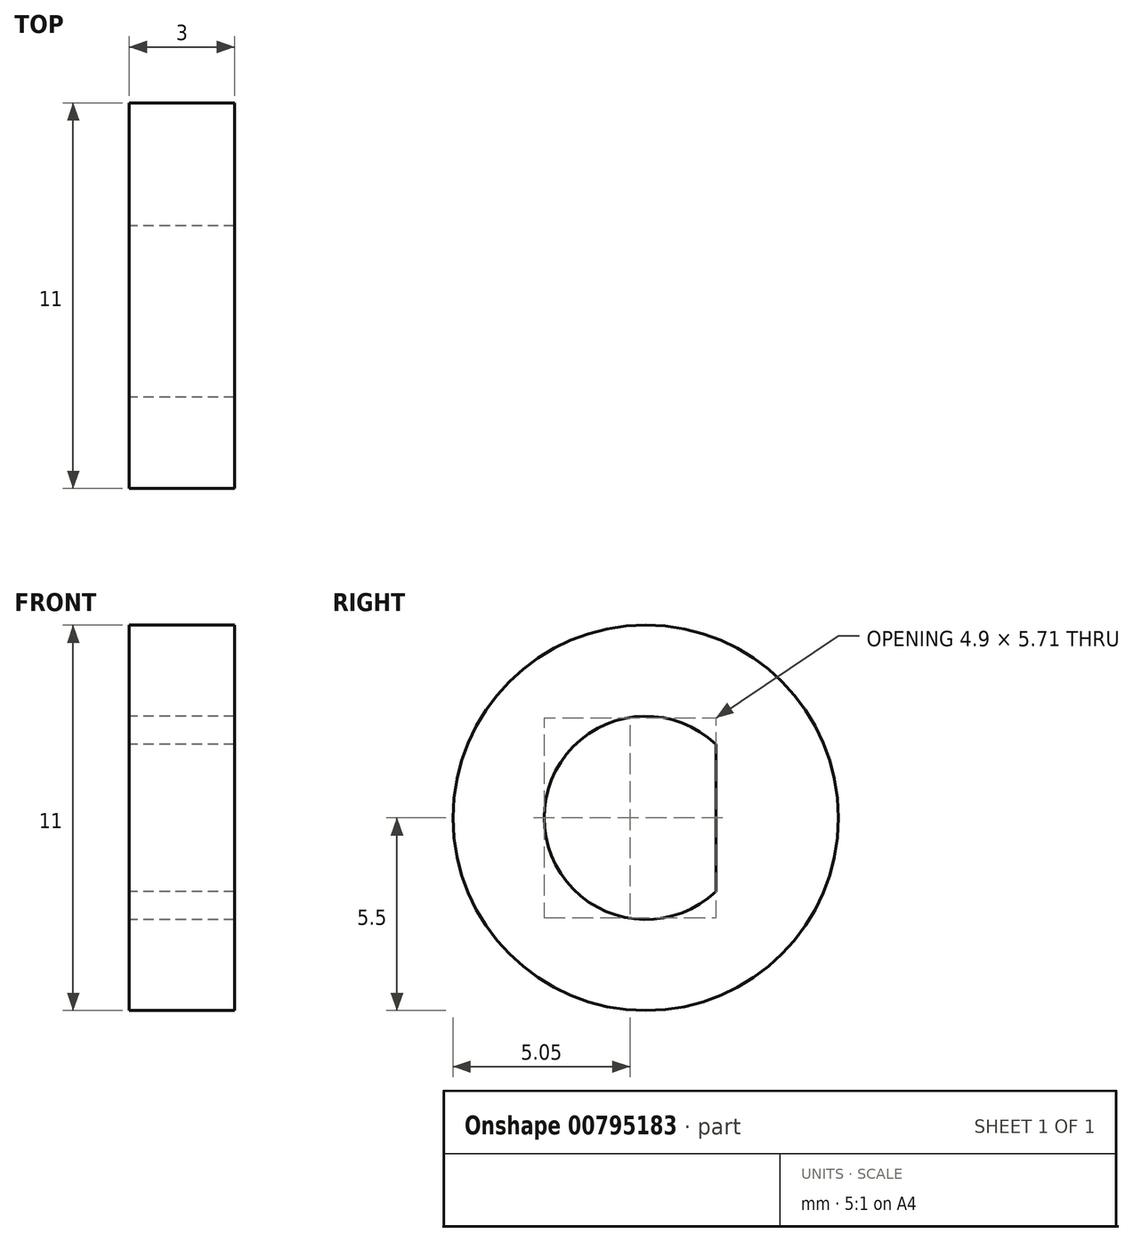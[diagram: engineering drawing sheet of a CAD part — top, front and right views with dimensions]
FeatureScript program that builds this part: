
annotation { "Feature Type Name" : "Feature", "Feature Type Description" : "" }
export const myFeature = defineFeature(function(context is Context, id is Id, definition is map)
    precondition{}
    {
        {
            var Q0;
            Q0=qCreatedBy(makeId("Right.planeOp"),FACE);
            var sketch = newSketch(context, id + "F0", { "sketchPlane" : qUnion([Q0])});
            skCircle(sketch, "E0", {"center": v(0, 0) * mm, "radius": 10.5 * mm, "construction": true});
            skCircle(sketch, "E1", {"center": v(0, 0) * mm, "radius": 2.9 * mm});
            skLineSegment(sketch, "E2", {"start": v(0, 0) * mm, "end": v(0, 12.5) * mm, "construction": true});
            skLineSegment(sketch, "E3", {"start": v(0, 12.5) * mm, "end": v(0.84, 10.47) * mm});
            skCircle(sketch, "E4", {"center": v(0, 0) * mm, "radius": 12.5 * mm, "construction": true});
            skLineSegment(sketch, "E5", {"start": v(0.84, 10.47) * mm, "end": v(2, 12.34) * mm});
            skLineSegment(sketch, "E6", {"start": v(2, 12.34) * mm, "end": v(0, 0) * mm, "construction": true});
            skLineSegment(sketch, "E7.1.0", {"start": v(-2, 12.34) * mm, "end": v(-0.84, 10.47) * mm});
            skLineSegment(sketch, "E7.1.1", {"start": v(-0.84, 10.47) * mm, "end": v(0, 12.5) * mm});
            skLineSegment(sketch, "E7.2.0", {"start": v(-3.94, 11.86) * mm, "end": v(-2.5, 10.2) * mm});
            skLineSegment(sketch, "E7.2.1", {"start": v(-2.5, 10.2) * mm, "end": v(-2, 12.34) * mm});
            skLineSegment(sketch, "E7.3.0", {"start": v(-5.77, 11.07) * mm, "end": v(-4.09, 9.66) * mm});
            skLineSegment(sketch, "E7.3.1", {"start": v(-4.09, 9.66) * mm, "end": v(-3.94, 11.86) * mm});
            skLineSegment(sketch, "E7.4.0", {"start": v(-7.46, 10) * mm, "end": v(-5.57, 8.88) * mm});
            skLineSegment(sketch, "E7.4.1", {"start": v(-5.57, 8.88) * mm, "end": v(-5.77, 11.07) * mm});
            skLineSegment(sketch, "E7.5.0", {"start": v(-8.96, 8.68) * mm, "end": v(-6.91, 7.87) * mm});
            skLineSegment(sketch, "E7.5.1", {"start": v(-6.91, 7.87) * mm, "end": v(-7.46, 10) * mm});
            skLineSegment(sketch, "E7.6.0", {"start": v(-10.23, 7.13) * mm, "end": v(-8.07, 6.66) * mm});
            skLineSegment(sketch, "E7.6.1", {"start": v(-8.07, 6.66) * mm, "end": v(-8.96, 8.68) * mm});
            skLineSegment(sketch, "E7.7.0", {"start": v(-11.22, 5.4) * mm, "end": v(-9.03, 5.28) * mm});
            skLineSegment(sketch, "E7.7.1", {"start": v(-9.03, 5.28) * mm, "end": v(-10.23, 7.13) * mm});
            skLineSegment(sketch, "E7.8.0", {"start": v(-11.93, 3.52) * mm, "end": v(-9.75, 3.77) * mm});
            skLineSegment(sketch, "E7.8.1", {"start": v(-9.75, 3.77) * mm, "end": v(-11.22, 5.4) * mm});
            skLineSegment(sketch, "E7.9.0", {"start": v(-12.33, 1.56) * mm, "end": v(-10.21, 2.15) * mm});
            skLineSegment(sketch, "E7.9.1", {"start": v(-10.21, 2.15) * mm, "end": v(-11.93, 3.52) * mm});
            skLineSegment(sketch, "E7.10.0", {"start": v(-12.41, -0.43) * mm, "end": v(-10.41, 0.49) * mm});
            skLineSegment(sketch, "E7.10.1", {"start": v(-10.41, 0.49) * mm, "end": v(-12.33, 1.56) * mm});
            skLineSegment(sketch, "E7.11.0", {"start": v(-12.17, -2.42) * mm, "end": v(-10.34, -1.19) * mm});
            skLineSegment(sketch, "E7.11.1", {"start": v(-10.34, -1.19) * mm, "end": v(-12.41, -0.43) * mm});
            skLineSegment(sketch, "E7.12.0", {"start": v(-11.61, -4.34) * mm, "end": v(-10, -2.83) * mm});
            skLineSegment(sketch, "E7.12.1", {"start": v(-10, -2.83) * mm, "end": v(-12.17, -2.42) * mm});
            skLineSegment(sketch, "E7.13.0", {"start": v(-10.75, -6.15) * mm, "end": v(-9.41, -4.4) * mm});
            skLineSegment(sketch, "E7.13.1", {"start": v(-9.41, -4.4) * mm, "end": v(-11.61, -4.34) * mm});
            skLineSegment(sketch, "E7.14.0", {"start": v(-9.62, -7.8) * mm, "end": v(-8.57, -5.85) * mm});
            skLineSegment(sketch, "E7.14.1", {"start": v(-8.57, -5.85) * mm, "end": v(-10.75, -6.15) * mm});
            skLineSegment(sketch, "E7.15.0", {"start": v(-8.23, -9.23) * mm, "end": v(-7.51, -7.15) * mm});
            skLineSegment(sketch, "E7.15.1", {"start": v(-7.51, -7.15) * mm, "end": v(-9.62, -7.8) * mm});
            skLineSegment(sketch, "E7.16.0", {"start": v(-6.63, -10.43) * mm, "end": v(-6.25, -8.27) * mm});
            skLineSegment(sketch, "E7.16.1", {"start": v(-6.25, -8.27) * mm, "end": v(-8.23, -9.23) * mm});
            skLineSegment(sketch, "E7.17.0", {"start": v(-4.86, -11.36) * mm, "end": v(-4.84, -9.16) * mm});
            skLineSegment(sketch, "E7.17.1", {"start": v(-4.84, -9.16) * mm, "end": v(-6.63, -10.43) * mm});
            skLineSegment(sketch, "E7.18.0", {"start": v(-2.96, -12) * mm, "end": v(-3.3, -9.82) * mm});
            skLineSegment(sketch, "E7.18.1", {"start": v(-3.3, -9.82) * mm, "end": v(-4.86, -11.36) * mm});
            skLineSegment(sketch, "E7.19.0", {"start": v(-0.99, -12.32) * mm, "end": v(-1.66, -10.22) * mm});
            skLineSegment(sketch, "E7.19.1", {"start": v(-1.66, -10.22) * mm, "end": v(-2.96, -12) * mm});
            skLineSegment(sketch, "E7.20.0", {"start": v(1.01, -12.31) * mm, "end": v(0.01, -10.35) * mm});
            skLineSegment(sketch, "E7.20.1", {"start": v(0.01, -10.35) * mm, "end": v(-0.99, -12.32) * mm});
            skLineSegment(sketch, "E7.21.0", {"start": v(2.99, -12) * mm, "end": v(1.68, -10.22) * mm});
            skLineSegment(sketch, "E7.21.1", {"start": v(1.68, -10.22) * mm, "end": v(1.01, -12.31) * mm});
            skLineSegment(sketch, "E7.22.0", {"start": v(4.88, -11.36) * mm, "end": v(3.31, -9.82) * mm});
            skLineSegment(sketch, "E7.22.1", {"start": v(3.31, -9.82) * mm, "end": v(2.99, -12) * mm});
            skLineSegment(sketch, "E7.23.0", {"start": v(6.65, -10.43) * mm, "end": v(4.86, -9.16) * mm});
            skLineSegment(sketch, "E7.23.1", {"start": v(4.86, -9.16) * mm, "end": v(4.88, -11.36) * mm});
            skLineSegment(sketch, "E7.24.0", {"start": v(8.25, -9.23) * mm, "end": v(6.27, -8.26) * mm});
            skLineSegment(sketch, "E7.24.1", {"start": v(6.27, -8.26) * mm, "end": v(6.65, -10.43) * mm});
            skLineSegment(sketch, "E7.25.0", {"start": v(9.64, -7.78) * mm, "end": v(7.53, -7.15) * mm});
            skLineSegment(sketch, "E7.25.1", {"start": v(7.53, -7.15) * mm, "end": v(8.25, -9.23) * mm});
            skLineSegment(sketch, "E7.26.0", {"start": v(10.77, -6.14) * mm, "end": v(8.6, -5.85) * mm});
            skLineSegment(sketch, "E7.26.1", {"start": v(8.6, -5.85) * mm, "end": v(9.64, -7.78) * mm});
            skLineSegment(sketch, "E7.27.0", {"start": v(11.63, -4.33) * mm, "end": v(9.43, -4.4) * mm});
            skLineSegment(sketch, "E7.27.1", {"start": v(9.43, -4.4) * mm, "end": v(10.77, -6.14) * mm});
            skLineSegment(sketch, "E7.28.0", {"start": v(12.18, -2.4) * mm, "end": v(10.02, -2.82) * mm});
            skLineSegment(sketch, "E7.28.1", {"start": v(10.02, -2.82) * mm, "end": v(11.63, -4.33) * mm});
            skLineSegment(sketch, "E7.29.0", {"start": v(12.42, -0.42) * mm, "end": v(10.36, -1.18) * mm});
            skLineSegment(sketch, "E7.29.1", {"start": v(10.36, -1.18) * mm, "end": v(12.18, -2.4) * mm});
            skLineSegment(sketch, "E7.30.0", {"start": v(12.34, 1.58) * mm, "end": v(10.42, 0.5) * mm});
            skLineSegment(sketch, "E7.30.1", {"start": v(10.42, 0.5) * mm, "end": v(12.42, -0.42) * mm});
            skLineSegment(sketch, "E7.31.0", {"start": v(11.94, 3.54) * mm, "end": v(10.22, 2.16) * mm});
            skLineSegment(sketch, "E7.31.1", {"start": v(10.22, 2.16) * mm, "end": v(12.34, 1.58) * mm});
            skLineSegment(sketch, "E7.32.0", {"start": v(11.23, 5.4) * mm, "end": v(9.75, 3.77) * mm});
            skLineSegment(sketch, "E7.32.1", {"start": v(9.75, 3.77) * mm, "end": v(11.94, 3.54) * mm});
            skLineSegment(sketch, "E7.33.0", {"start": v(10.23, 7.14) * mm, "end": v(9.03, 5.3) * mm});
            skLineSegment(sketch, "E7.33.1", {"start": v(9.03, 5.3) * mm, "end": v(11.23, 5.4) * mm});
            skLineSegment(sketch, "E7.34.0", {"start": v(8.96, 8.69) * mm, "end": v(8.08, 6.67) * mm});
            skLineSegment(sketch, "E7.34.1", {"start": v(8.08, 6.67) * mm, "end": v(10.23, 7.14) * mm});
            skLineSegment(sketch, "E7.35.0", {"start": v(7.47, 10.01) * mm, "end": v(6.92, 7.88) * mm});
            skLineSegment(sketch, "E7.35.1", {"start": v(6.92, 7.88) * mm, "end": v(8.96, 8.69) * mm});
            skLineSegment(sketch, "E7.36.0", {"start": v(5.78, 11.08) * mm, "end": v(5.57, 8.89) * mm});
            skLineSegment(sketch, "E7.36.1", {"start": v(5.57, 8.89) * mm, "end": v(7.47, 10.01) * mm});
            skLineSegment(sketch, "E7.37.0", {"start": v(3.94, 11.86) * mm, "end": v(4.09, 9.67) * mm});
            skLineSegment(sketch, "E7.37.1", {"start": v(4.09, 9.67) * mm, "end": v(5.78, 11.08) * mm});
            skLineSegment(sketch, "E7.38.0", {"start": v(2, 12.34) * mm, "end": v(2.5, 10.2) * mm});
            skLineSegment(sketch, "E7.38.1", {"start": v(2.5, 10.2) * mm, "end": v(3.94, 11.86) * mm});
            skPoint(sketch, "E7.center", {"position": v(0, 0.07) * mm});
            skSolve(sketch);
        }
        {
            var Q0;
            Q0=makeQuery(id+"F0.imprint","IMPRINT",FACE,{"disambiguationData":[TD([[makeQuery(id+"F0.imprint","IMPRINT",EDGE,{"derivedFrom":sQuery(id+"F0.wireOp",EDGE,"E1")}),-1.0]])]});
            extrude(context, id + "F1", {"entities" : qUnion([Q0]), "depth" : 3 * mm, "offsetDistance" : 25.4 * mm});
        }
        {
            var Q0;
            Q0=qCreatedBy(makeId("Right.planeOp"),FACE);
            var sketch = newSketch(context, id + "F2", { "sketchPlane" : qUnion([Q0])});
            skLineSegment(sketch, "E8", {"start": v(2, 2.1) * mm, "end": v(2, -2.1) * mm});
            skArc(sketch, "E9", {"start": v(2, -2.1) * mm, "mid": v(2.9, 0) * mm, "end": v(2, 2.1) * mm});
            skSolve(sketch);
        }
        {
            var Q0;
            Q0=qSketchRegion(id+"F2",true);
            extrude(context, id + "F3", {"entities" : qUnion([Q0]), "operationType" : NewBodyOperationType.ADD, "depth" : 3 * mm, "offsetDistance" : 25.4 * mm});
        }
        {
            var Q0;
            Q0=qCreatedBy(makeId("Right.planeOp"),FACE);
            var sketch = newSketch(context, id + "F4", { "sketchPlane" : qUnion([Q0])});
            skCircle(sketch, "E10", {"center": v(0, 0) * mm, "radius": 5.5 * mm});
            skCircle(sketch, "E11", {"center": v(0, 0) * mm, "radius": 14.86 * mm});
            skSolve(sketch);
        }
        {
            var Q0;
            Q0=makeQuery(id+"F4.imprint","IMPRINT",FACE,{"disambiguationData":[TD([[makeQuery(id+"F4.imprint","IMPRINT",EDGE,{"derivedFrom":sQuery(id+"F4.wireOp",EDGE,"E10")}),-1.0]])]});
            extrude(context, id + "F5", {"entities" : qUnion([Q0]), "operationType" : NewBodyOperationType.REMOVE, "depth" : 25.4 * mm, "offsetDistance" : 25.4 * mm});
        }
    });
